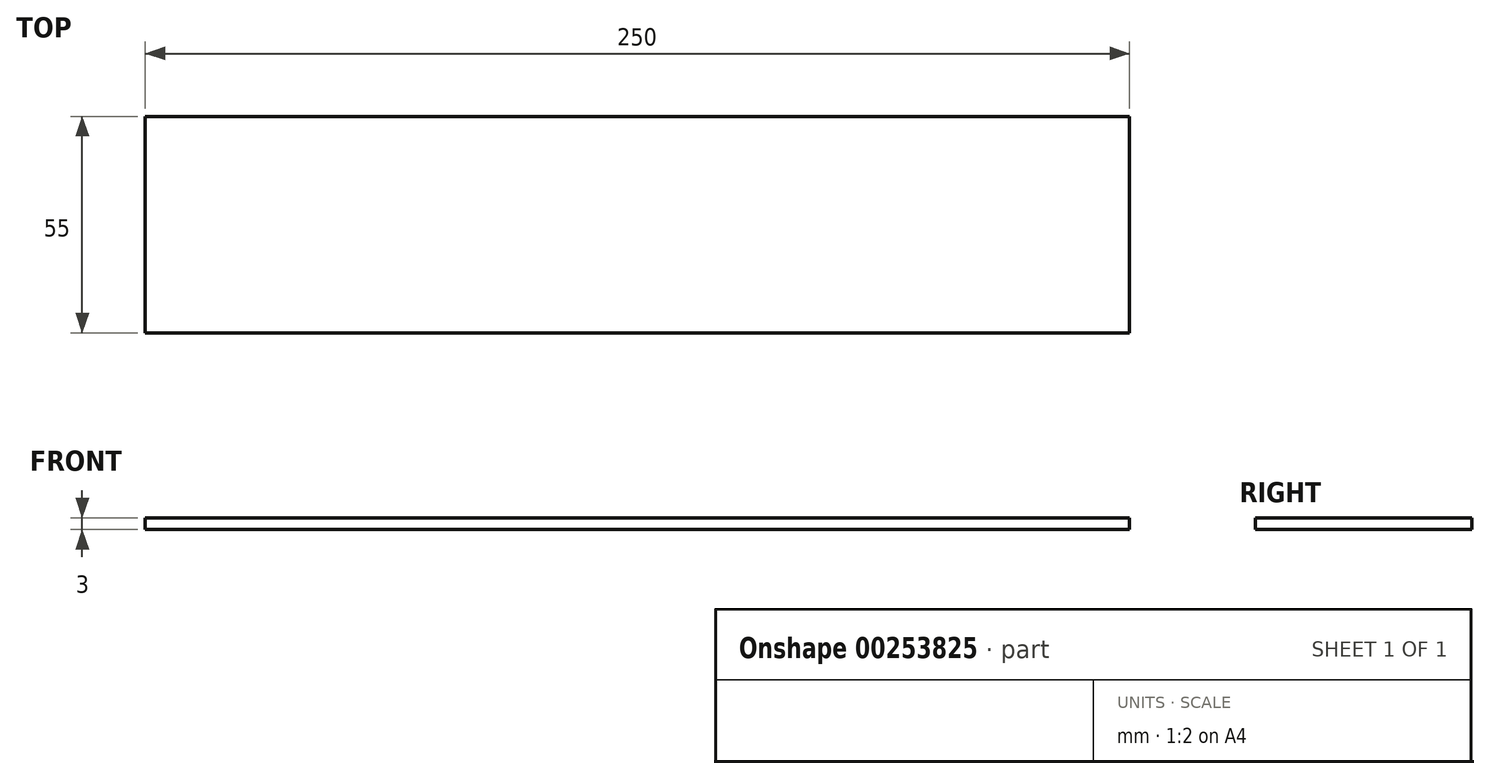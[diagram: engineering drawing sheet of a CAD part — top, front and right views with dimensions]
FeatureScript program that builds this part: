
annotation { "Feature Type Name" : "Feature", "Feature Type Description" : "" }
export const myFeature = defineFeature(function(context is Context, id is Id, definition is map)
    precondition{}
    {
        {
            var Q0;
            Q0=qCreatedBy(makeId("Top.planeOp"),FACE);
            var sketch = newSketch(context, id + "F0", { "sketchPlane" : qUnion([Q0])});
            skLineSegment(sketch, "E0", {"start": v(125, -27.5) * mm, "end": v(-125, -27.5) * mm});
            skLineSegment(sketch, "E1", {"start": v(-125, -27.5) * mm, "end": v(-125, 27.5) * mm});
            skLineSegment(sketch, "E2", {"start": v(-125, 27.5) * mm, "end": v(125, 27.5) * mm});
            skLineSegment(sketch, "E3", {"start": v(125, 27.5) * mm, "end": v(125, -27.5) * mm});
            skSolve(sketch);
        }
        {
            var Q0;
            Q0=makeQuery(id+"F0.imprint","IMPRINT",FACE,{"disambiguationData":[TD([[makeQuery(id+"F0.imprint","IMPRINT",EDGE,{"derivedFrom":sQuery(id+"F0.wireOp",EDGE,"E0")}),-1.0]])]});
            extrude(context, id + "F1", {"entities" : qUnion([Q0]), "depth" : 3 * mm});
        }
    });
